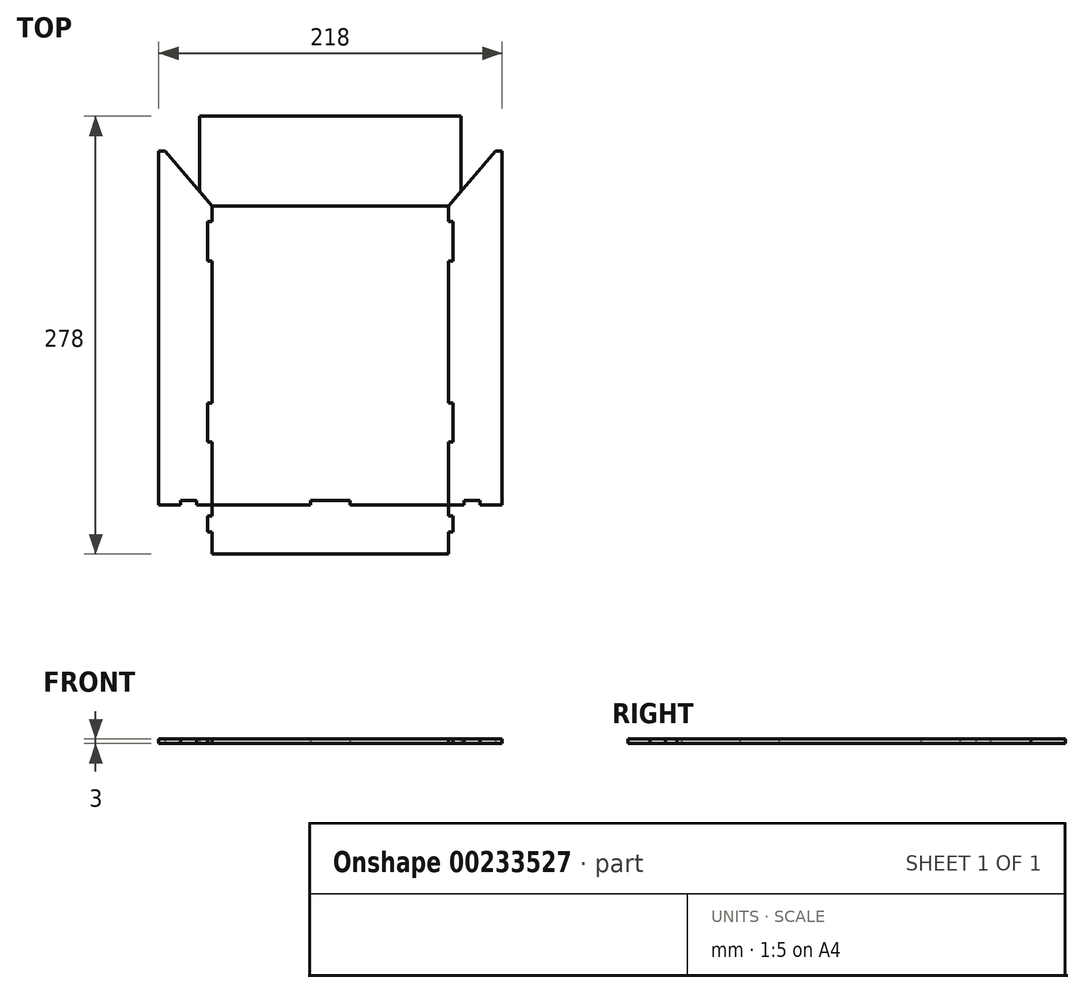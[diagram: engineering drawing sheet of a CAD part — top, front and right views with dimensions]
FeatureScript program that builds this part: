
annotation { "Feature Type Name" : "Feature", "Feature Type Description" : "" }
export const myFeature = defineFeature(function(context is Context, id is Id, definition is map)
    precondition{}
    {
        {
            var Q0;
            Q0=qCreatedBy(makeId("Top.planeOp"),FACE);
            var sketch = newSketch(context, id + "F0", { "sketchPlane" : qUnion([Q0])});
            skLineSegment(sketch, "E0", {"start": v(-12.5, 0) * mm, "end": v(-75, 0) * mm});
            skLineSegment(sketch, "E1", {"start": v(-75, 0) * mm, "end": v(-75, 40) * mm});
            skLineSegment(sketch, "E2", {"start": v(-75, 190) * mm, "end": v(0, 190) * mm});
            skLineSegment(sketch, "E3", {"start": v(0, 0) * mm, "end": v(0, 280.68) * mm, "construction": true});
            skLineSegment(sketch, "E4", {"start": v(-105, 0) * mm, "end": v(-95, 0) * mm});
            skLineSegment(sketch, "E5", {"start": v(-75, 0) * mm, "end": v(-75, -7) * mm});
            skLineSegment(sketch, "E6", {"start": v(-75, -31) * mm, "end": v(0, -31) * mm});
            skLineSegment(sketch, "E7", {"start": v(-78, 180) * mm, "end": v(-75, 180) * mm});
            skLineSegment(sketch, "E8", {"start": v(-78, 180) * mm, "end": v(-78, 155) * mm});
            skLineSegment(sketch, "E9", {"start": v(-75, 155) * mm, "end": v(-78, 155) * mm});
            skLineSegment(sketch, "E10", {"start": v(-78, 65) * mm, "end": v(-75, 65) * mm});
            skLineSegment(sketch, "E11", {"start": v(-78, 65) * mm, "end": v(-78, 40) * mm});
            skLineSegment(sketch, "E12", {"start": v(-75, 40) * mm, "end": v(-78, 40) * mm});
            skLineSegment(sketch, "E13.trimOffspring", {"start": v(-75, 65) * mm, "end": v(-75, 155) * mm});
            skLineSegment(sketch, "E14", {"start": v(-12.5, 0) * mm, "end": v(-12.5, 3) * mm});
            skLineSegment(sketch, "E15", {"start": v(-12.5, 3) * mm, "end": v(0, 3) * mm});
            skLineSegment(sketch, "E16", {"start": v(-95, 0) * mm, "end": v(-95, 3) * mm});
            skLineSegment(sketch, "E17", {"start": v(-95, 3) * mm, "end": v(-85, 3) * mm});
            skLineSegment(sketch, "E18", {"start": v(-85, 3) * mm, "end": v(-85, 0) * mm});
            skLineSegment(sketch, "E19", {"start": v(-90, 3) * mm, "end": v(-90, 0) * mm, "construction": true});
            skLineSegment(sketch, "E20", {"start": v(-75, -17) * mm, "end": v(-78, -17) * mm});
            skLineSegment(sketch, "E21", {"start": v(-78, -17) * mm, "end": v(-78, -7) * mm});
            skLineSegment(sketch, "E22", {"start": v(-78, -7) * mm, "end": v(-75, -7) * mm});
            skLineSegment(sketch, "E23", {"start": v(-75, -12) * mm, "end": v(-78, -12) * mm, "construction": true});
            skLineSegment(sketch, "E24.trimOffspring", {"start": v(-85, 0) * mm, "end": v(-75, 0) * mm});
            skLineSegment(sketch, "E25.trimOffspring", {"start": v(-75, -17) * mm, "end": v(-75, -31) * mm});
            skLineSegment(sketch, "E26.MirrorCS", {"start": v(75, -12) * mm, "end": v(78, -12) * mm, "construction": true});
            skLineSegment(sketch, "E27.MirrorCS", {"start": v(90, 3) * mm, "end": v(90, 0) * mm, "construction": true});
            skLineSegment(sketch, "E28.MirrorCS", {"start": v(85, 0) * mm, "end": v(75, 0) * mm});
            skLineSegment(sketch, "E29.MirrorCS", {"start": v(95, 0) * mm, "end": v(95, 3) * mm});
            skLineSegment(sketch, "E30.MirrorCS", {"start": v(85, 3) * mm, "end": v(85, 0) * mm});
            skLineSegment(sketch, "E31.MirrorCS", {"start": v(95, 3) * mm, "end": v(85, 3) * mm});
            skLineSegment(sketch, "E32.MirrorCS", {"start": v(75, -17) * mm, "end": v(78, -17) * mm});
            skLineSegment(sketch, "E33.MirrorCS", {"start": v(78, -7) * mm, "end": v(75, -7) * mm});
            skLineSegment(sketch, "E34.MirrorCS", {"start": v(78, -17) * mm, "end": v(78, -7) * mm});
            skLineSegment(sketch, "E35.MirrorCS", {"start": v(12.5, 0) * mm, "end": v(12.5, 3) * mm});
            skLineSegment(sketch, "E36.MirrorCS", {"start": v(12.5, 3) * mm, "end": v(0, 3) * mm});
            skLineSegment(sketch, "E37.MirrorCS", {"start": v(78, 180) * mm, "end": v(75, 180) * mm});
            skLineSegment(sketch, "E38.MirrorCS", {"start": v(75, 155) * mm, "end": v(78, 155) * mm});
            skLineSegment(sketch, "E39.MirrorCS", {"start": v(105, 0) * mm, "end": v(95, 0) * mm});
            skLineSegment(sketch, "E40.MirrorCS", {"start": v(75, 0) * mm, "end": v(75, -7) * mm});
            skLineSegment(sketch, "E41.MirrorCS", {"start": v(75, 40) * mm, "end": v(78, 40) * mm});
            skLineSegment(sketch, "E42.MirrorCS", {"start": v(78, 65) * mm, "end": v(75, 65) * mm});
            skLineSegment(sketch, "E43.MirrorCS", {"start": v(75, -17) * mm, "end": v(75, -31) * mm});
            skLineSegment(sketch, "E44.MirrorCS", {"start": v(75, 65) * mm, "end": v(75, 155) * mm});
            skLineSegment(sketch, "E45.MirrorCS", {"start": v(78, 65) * mm, "end": v(78, 40) * mm});
            skLineSegment(sketch, "E46.MirrorCS", {"start": v(75, 190) * mm, "end": v(0, 190) * mm});
            skLineSegment(sketch, "E47.MirrorCS", {"start": v(78, 180) * mm, "end": v(78, 155) * mm});
            skLineSegment(sketch, "E48.MirrorCS", {"start": v(12.5, 0) * mm, "end": v(75, 0) * mm});
            skLineSegment(sketch, "E49.MirrorCS", {"start": v(75, 0) * mm, "end": v(75, 40) * mm});
            skLineSegment(sketch, "E50.MirrorCS", {"start": v(75, -31) * mm, "end": v(0, -31) * mm});
            skLineSegment(sketch, "E51", {"start": v(-75, 180) * mm, "end": v(-75, 190) * mm});
            skLineSegment(sketch, "E52", {"start": v(-75, 190) * mm, "end": v(-105, 225) * mm});
            skLineSegment(sketch, "E53", {"start": v(75, 180) * mm, "end": v(75, 190) * mm});
            skLineSegment(sketch, "E54", {"start": v(75, 190) * mm, "end": v(105, 225) * mm});
            skLineSegment(sketch, "E55", {"start": v(-83, 247) * mm, "end": v(83, 247) * mm});
            skLineSegment(sketch, "E56", {"start": v(-83, 247) * mm, "end": v(-83, 199.33) * mm});
            skLineSegment(sketch, "E57", {"start": v(83, 247) * mm, "end": v(83, 199.33) * mm});
            skLineSegment(sketch, "E58", {"start": v(-105, 225) * mm, "end": v(-109, 225) * mm});
            skLineSegment(sketch, "E59", {"start": v(-109, 225) * mm, "end": v(-109, 0) * mm});
            skLineSegment(sketch, "E60", {"start": v(-109, 0) * mm, "end": v(-105, 0) * mm});
            skLineSegment(sketch, "E61.MirrorCS", {"start": v(105, 225) * mm, "end": v(109, 225) * mm});
            skLineSegment(sketch, "E62.MirrorCS", {"start": v(109, 0) * mm, "end": v(105, 0) * mm});
            skLineSegment(sketch, "E63.MirrorCS", {"start": v(109, 225) * mm, "end": v(109, 0) * mm});
            skSolve(sketch);
        }
        {
            var Q0;
            Q0=makeQuery(id+"F0.imprint","IMPRINT",FACE,{"disambiguationData":[TD([[makeQuery(id+"F0.imprint","IMPRINT",EDGE,{"derivedFrom":sQuery(id+"F0.wireOp",EDGE,"E28.MirrorCS")}),-1.0]])]});
            var Q1;
            Q1=makeQuery(id+"F0.imprint","IMPRINT",FACE,{"disambiguationData":[TD([[makeQuery(id+"F0.imprint","IMPRINT",EDGE,{"derivedFrom":sQuery(id+"F0.wireOp",EDGE,"E0")}),1.0]])]});
            var Q2;
            Q2=makeQuery(id+"F0.imprint","IMPRINT",FACE,{"disambiguationData":[TD([[makeQuery(id+"F0.imprint","IMPRINT",EDGE,{"derivedFrom":sQuery(id+"F0.wireOp",EDGE,"E1")}),1.0]])]});
            extrude(context, id + "F1", {"entities" : qUnion([Q0, Q1, Q2]), "depth" : 3 * mm});
        }
        {
            var Q0;
            Q0=makeQuery(id+"F0.imprint","IMPRINT",FACE,{"disambiguationData":[TD([[makeQuery(id+"F0.imprint","IMPRINT",EDGE,{"derivedFrom":sQuery(id+"F0.wireOp",EDGE,"E0")}),-1.0]])]});
            extrude(context, id + "F2", {"entities" : qUnion([Q0]), "depth" : 3 * mm});
        }
        {
            var Q0;
            Q0=makeQuery(id+"F0.imprint","IMPRINT",FACE,{"disambiguationData":[TD([[makeQuery(id+"F0.imprint","IMPRINT",EDGE,{"derivedFrom":sQuery(id+"F0.wireOp",EDGE,"E2")}),1.0]])]});
            extrude(context, id + "F3", {"entities" : qUnion([Q0]), "depth" : 3 * mm});
        }
    });
